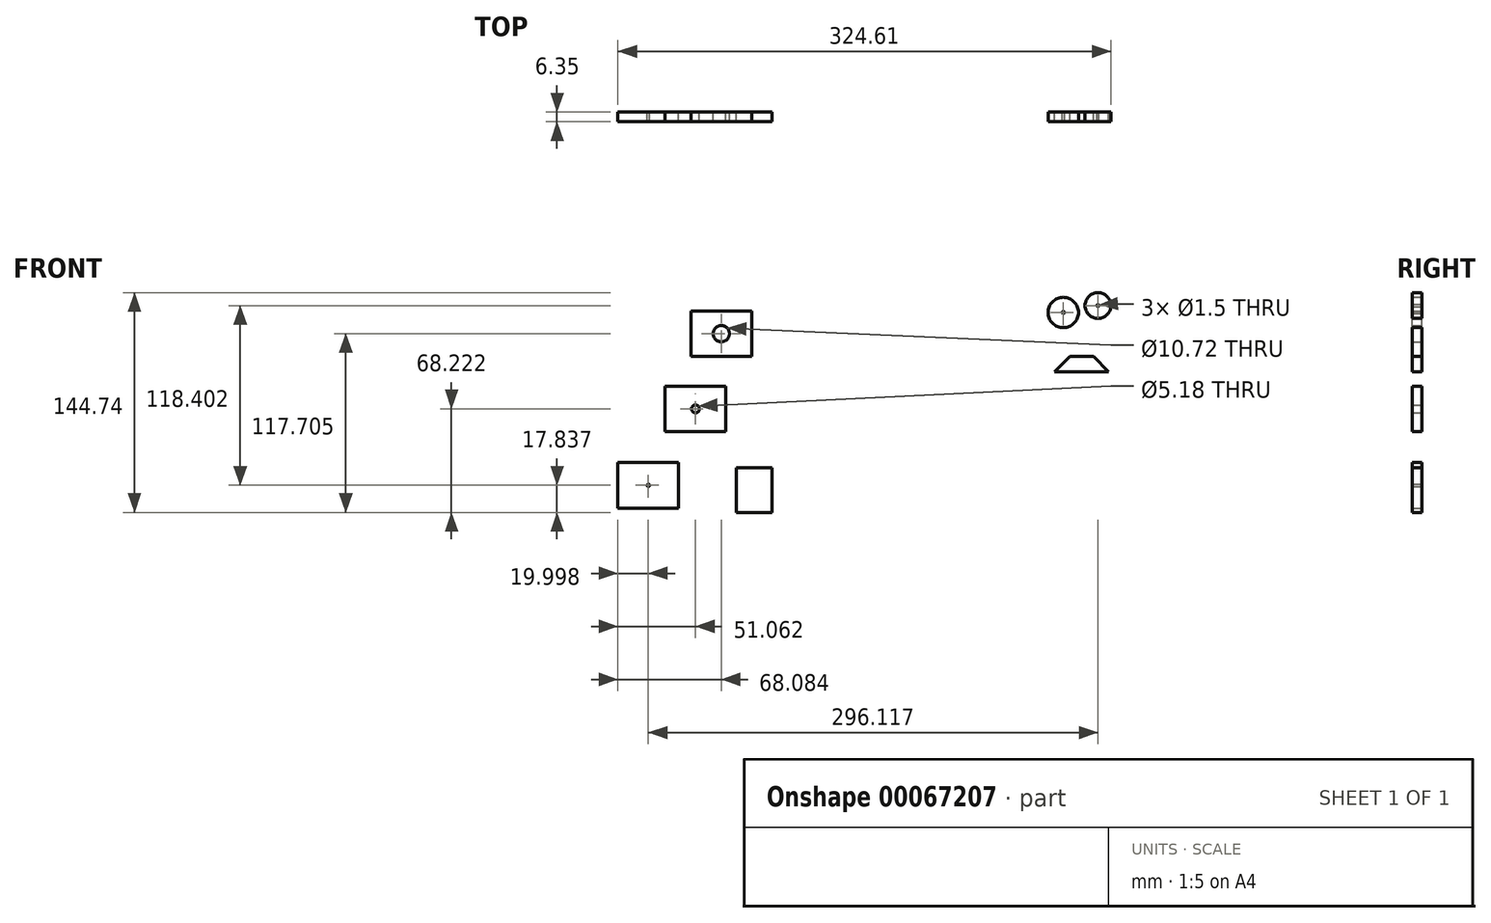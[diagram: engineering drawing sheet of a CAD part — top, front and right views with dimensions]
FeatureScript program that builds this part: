
annotation { "Feature Type Name" : "Feature", "Feature Type Description" : "" }
export const myFeature = defineFeature(function(context is Context, id is Id, definition is map)
    precondition{}
    {
        {
            var Q0;
            Q0=qCreatedBy(makeId("Front.planeOp"),FACE);
            var sketch = newSketch(context, id + "F0", { "sketchPlane" : qUnion([Q0])});
            skLineSegment(sketch, "E0.bottom", {"start": v(-105.03, 28.14) * mm, "end": v(-145.03, 28.14) * mm});
            skLineSegment(sketch, "E0.top", {"start": v(-105.03, 58.14) * mm, "end": v(-145.03, 58.14) * mm});
            skLineSegment(sketch, "E0.left", {"start": v(-105.03, 28.14) * mm, "end": v(-105.03, 58.14) * mm});
            skLineSegment(sketch, "E0.right", {"start": v(-145.03, 28.14) * mm, "end": v(-145.03, 58.14) * mm});
            skPoint(sketch, "E0.middle", {"position": v(-125.03, 43.14) * mm});
            skCircle(sketch, "E1", {"center": v(-125.03, 43.14) * mm, "radius": 5.36 * mm});
            skLineSegment(sketch, "E2.bottom", {"start": v(-122.05, -21.35) * mm, "end": v(-162.05, -21.35) * mm});
            skLineSegment(sketch, "E2.top", {"start": v(-122.05, 8.65) * mm, "end": v(-162.05, 8.65) * mm});
            skLineSegment(sketch, "E2.left", {"start": v(-122.05, -21.35) * mm, "end": v(-122.05, 8.65) * mm});
            skLineSegment(sketch, "E2.right", {"start": v(-162.05, -21.35) * mm, "end": v(-162.05, 8.65) * mm});
            skPoint(sketch, "E2.middle", {"position": v(-142.05, -6.35) * mm});
            skCircle(sketch, "E3", {"center": v(-142.05, -6.35) * mm, "radius": 2.6 * mm});
            skLineSegment(sketch, "E4.bottom", {"start": v(-153.11, -71.73) * mm, "end": v(-193.11, -71.73) * mm});
            skLineSegment(sketch, "E4.top", {"start": v(-153.11, -41.73) * mm, "end": v(-193.11, -41.73) * mm});
            skLineSegment(sketch, "E4.left", {"start": v(-153.11, -71.73) * mm, "end": v(-153.11, -41.73) * mm});
            skLineSegment(sketch, "E4.right", {"start": v(-193.11, -71.73) * mm, "end": v(-193.11, -41.73) * mm});
            skPoint(sketch, "E4.middle", {"position": v(-173.11, -56.73) * mm});
            skLineSegment(sketch, "E5.bottom", {"start": v(-91.65, -74.57) * mm, "end": v(-115.3, -74.57) * mm});
            skLineSegment(sketch, "E5.top", {"start": v(-91.65, -45.22) * mm, "end": v(-115.3, -45.22) * mm});
            skLineSegment(sketch, "E5.left", {"start": v(-91.65, -74.57) * mm, "end": v(-91.65, -45.22) * mm});
            skLineSegment(sketch, "E5.right", {"start": v(-115.3, -74.57) * mm, "end": v(-115.3, -45.22) * mm});
            skPoint(sketch, "E5.middle", {"position": v(-103.47, -59.9) * mm});
            skCircle(sketch, "E6", {"center": v(-173.11, -56.73) * mm, "radius": 0.75 * mm});
            skCircle(sketch, "E7", {"center": v(100.17, 57.1) * mm, "radius": 10 * mm});
            skCircle(sketch, "E8", {"center": v(123, 61.67) * mm, "radius": 8.5 * mm});
            skLineSegment(sketch, "E9.bottom", {"start": v(130.1, 18.13) * mm, "end": v(94.46, 18.13) * mm});
            skLineSegment(sketch, "E9.top", {"start": v(130.1, 28.13) * mm, "end": v(94.46, 28.13) * mm});
            skLineSegment(sketch, "E9.left", {"start": v(130.1, 18.13) * mm, "end": v(130.1, 28.13) * mm});
            skLineSegment(sketch, "E9.right", {"start": v(94.46, 18.13) * mm, "end": v(94.46, 28.13) * mm});
            skPoint(sketch, "E9.middle", {"position": v(112.28, 23.13) * mm});
            skLineSegment(sketch, "E10", {"start": v(94.46, 18.13) * mm, "end": v(104.46, 28.13) * mm});
            skLineSegment(sketch, "E11", {"start": v(130.1, 18.13) * mm, "end": v(120.1, 28.13) * mm});
            skCircle(sketch, "E12", {"center": v(100.17, 57.1) * mm, "radius": 0.75 * mm});
            skCircle(sketch, "E13", {"center": v(123, 61.67) * mm, "radius": 0.75 * mm});
            skSolve(sketch);
        }
        {
            var Q0;
            Q0=makeQuery(id+"F0.imprint","IMPRINT",FACE,{"disambiguationData":[TD([[makeQuery(id+"F0.imprint","IMPRINT",EDGE,{"derivedFrom":sQuery(id+"F0.wireOp",EDGE,"E5.bottom")}),-1.0]])]});
            var Q1;
            Q1=makeQuery(id+"F0.imprint","IMPRINT",FACE,{"disambiguationData":[TD([[makeQuery(id+"F0.imprint","IMPRINT",EDGE,{"derivedFrom":sQuery(id+"F0.wireOp",EDGE,"E8")}),1.0]])]});
            var Q2;
            Q2=makeQuery(id+"F0.imprint","IMPRINT",FACE,{"disambiguationData":[TD([[makeQuery(id+"F0.imprint","IMPRINT",EDGE,{"derivedFrom":sQuery(id+"F0.wireOp",EDGE,"E0.bottom")}),-1.0]])]});
            var Q3;
            Q3=makeQuery(id+"F0.imprint","IMPRINT",FACE,{"disambiguationData":[TD([[makeQuery(id+"F0.imprint","IMPRINT",EDGE,{"derivedFrom":sQuery(id+"F0.wireOp",EDGE,"E2.bottom")}),-1.0]])]});
            var Q4;
            Q4=makeQuery(id+"F0.imprint","IMPRINT",FACE,{"disambiguationData":[TD([[makeQuery(id+"F0.imprint","IMPRINT",EDGE,{"derivedFrom":sQuery(id+"F0.wireOp",EDGE,"E4.bottom")}),-1.0]])]});
            var Q5;
            Q5=makeQuery(id+"F0.imprint","IMPRINT",FACE,{"disambiguationData":[TD([[makeQuery(id+"F0.imprint","IMPRINT",EDGE,{"derivedFrom":sQuery(id+"F0.wireOp",EDGE,"E7")}),1.0]])]});
            var Q6;
            Q6=makeQuery(id+"F0.imprint","IMPRINT",FACE,{"disambiguationData":[TD([[makeQuery(id+"F0.imprint","IMPRINT",EDGE,{"derivedFrom":sQuery(id+"F0.wireOp",EDGE,"E9.bottom")}),-1.0]])]});
            extrude(context, id + "F1", {"entities" : qUnion([Q0, Q1, Q2, Q3, Q4, Q5, Q6]), "depth" : 6.35 * mm});
        }
    });
